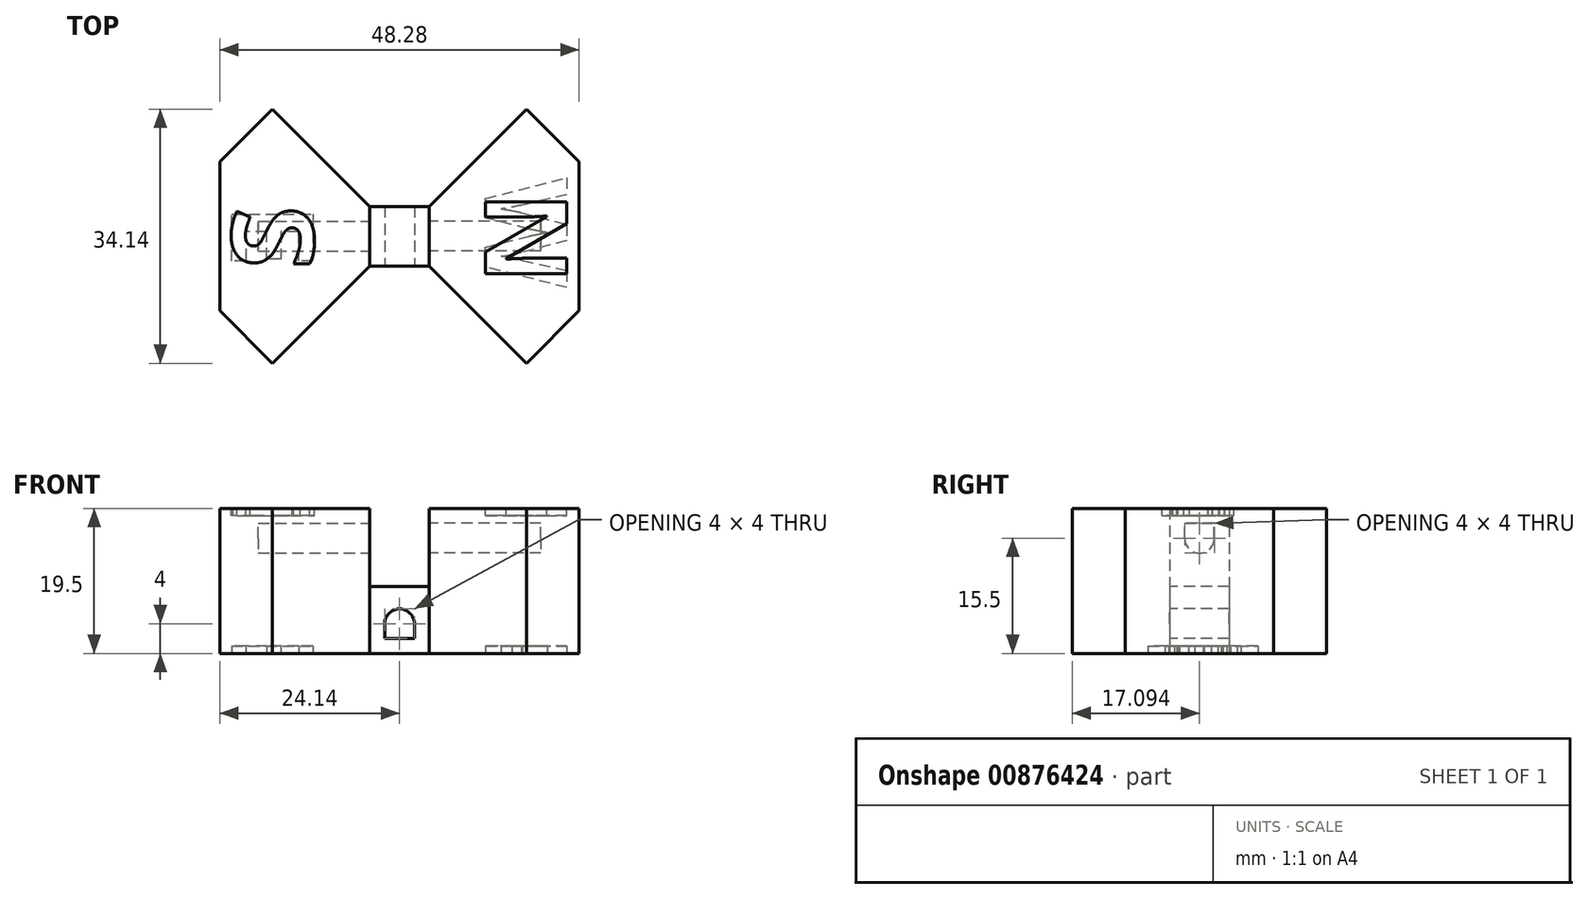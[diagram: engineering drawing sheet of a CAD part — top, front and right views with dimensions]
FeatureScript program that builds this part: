
annotation { "Feature Type Name" : "Feature", "Feature Type Description" : "" }
export const myFeature = defineFeature(function(context is Context, id is Id, definition is map)
    precondition{}
    {
        {
            var Q0;
            Q0=qCreatedBy(makeId("Top.planeOp"),FACE);
            var sketch = newSketch(context, id + "F0", { "sketchPlane" : qUnion([Q0])});
            skCircle(sketch, "E0.cCircle", {"center": v(0, 0) * mm, "radius": 24.14 * mm, "construction": true});
            skLineSegment(sketch, "E0.0", {"start": v(-24.14, 10) * mm, "end": v(-10, 24.14) * mm});
            skLineSegment(sketch, "E0.1", {"start": v(-10, 24.14) * mm, "end": v(10, 24.14) * mm});
            skLineSegment(sketch, "E0.2", {"start": v(10, 24.14) * mm, "end": v(24.14, 10) * mm});
            skLineSegment(sketch, "E0.3", {"start": v(24.14, 10) * mm, "end": v(24.14, -10) * mm});
            skLineSegment(sketch, "E0.4", {"start": v(24.14, -10) * mm, "end": v(10, -24.14) * mm});
            skLineSegment(sketch, "E0.5", {"start": v(10, -24.14) * mm, "end": v(-10, -24.14) * mm});
            skLineSegment(sketch, "E0.6", {"start": v(-10, -24.14) * mm, "end": v(-24.14, -10) * mm});
            skLineSegment(sketch, "E0.7", {"start": v(-24.14, -10) * mm, "end": v(-24.14, 10) * mm});
            skPoint(sketch, "E0.0.midPoint", {"position": v(-17.07, 17.07) * mm});
            skPoint(sketch, "E1", {"position": v(-17.07, -17.07) * mm});
            skPoint(sketch, "E2", {"position": v(17.07, 17.07) * mm});
            skPoint(sketch, "E3", {"position": v(17.07, -17.07) * mm});
            skLineSegment(sketch, "E4", {"start": v(-17.07, 17.07) * mm, "end": v(17.07, -17.07) * mm});
            skLineSegment(sketch, "E5", {"start": v(17.07, 17.07) * mm, "end": v(-17.07, -17.07) * mm});
            skPoint(sketch, "E6", {"position": v(0, 24.14) * mm});
            skPoint(sketch, "E7", {"position": v(24.14, 0) * mm});
            skPoint(sketch, "E8", {"position": v(0, -24.14) * mm});
            skLineSegment(sketch, "E9.bottom", {"start": v(-4, 4) * mm, "end": v(4, 4) * mm});
            skLineSegment(sketch, "E9.top", {"start": v(-4, -4) * mm, "end": v(4, -4) * mm});
            skLineSegment(sketch, "E9.left", {"start": v(-4, 4) * mm, "end": v(-4, -4) * mm});
            skLineSegment(sketch, "E9.right", {"start": v(4, 4) * mm, "end": v(4, -4) * mm});
            skPoint(sketch, "E10", {"position": v(0, 4) * mm});
            skPoint(sketch, "E11", {"position": v(-4, 0) * mm});
            skLineSegment(sketch, "E12", {"start": v(17.07, -17.07) * mm, "end": v(17.07, 17.07) * mm, "construction": true});
            skPoint(sketch, "E13", {"position": v(17.07, 0) * mm});
            skLineSegment(sketch, "E14", {"start": v(-17.07, -17.07) * mm, "end": v(-17.07, 17.07) * mm, "construction": true});
            skPoint(sketch, "E15", {"position": v(-17.07, 0) * mm});
            skSolve(sketch);
        }
        {
            var Q0;
            {var subQ4=sQuery(id+"F0.wireOp",EDGE,"E0.7");Q0=makeQuery(id+"F0.imprint","IMPRINT",FACE,{"disambiguationData":[TD([[makeQuery(id+"F0.imprint","IMPRINT",EDGE,{"derivedFrom":subQ4}),-1.0]])]});}
            var Q1;
            {var subQ1=sQuery(id+"F0.wireOp",EDGE,"E0.3");Q1=makeQuery(id+"F0.imprint","IMPRINT",FACE,{"disambiguationData":[TD([[makeQuery(id+"F0.imprint","IMPRINT",EDGE,{"derivedFrom":subQ1}),-1.0]])]});}
            extrude(context, id + "F1", {"entities" : qUnion([Q0, Q1]), "depth" : 19.5 * mm, "offsetDistance" : 25 * mm});
        }
        {
            var Q0;
            {var subQ0=sQuery(id+"F0.wireOp",EDGE,"E9.right");Q0=makeQuery(id+"F0.imprint","IMPRINT",FACE,{"disambiguationData":[TD([[makeQuery(id+"F0.imprint","IMPRINT",EDGE,{"derivedFrom":subQ0}),-1.0]])]});}
            var Q1;
            {var subQ0=sQuery(id+"F0.wireOp",EDGE,"E9.bottom");Q1=makeQuery(id+"F0.imprint","IMPRINT",FACE,{"disambiguationData":[TD([[makeQuery(id+"F0.imprint","IMPRINT",EDGE,{"derivedFrom":subQ0}),-1.0]])]});}
            var Q2;
            {var subQ0=sQuery(id+"F0.wireOp",EDGE,"E9.left");Q2=makeQuery(id+"F0.imprint","IMPRINT",FACE,{"disambiguationData":[TD([[makeQuery(id+"F0.imprint","IMPRINT",EDGE,{"derivedFrom":subQ0}),1.0]])]});}
            var Q3;
            {var subQ0=sQuery(id+"F0.wireOp",EDGE,"E9.top");Q3=makeQuery(id+"F0.imprint","IMPRINT",FACE,{"disambiguationData":[TD([[makeQuery(id+"F0.imprint","IMPRINT",EDGE,{"derivedFrom":subQ0}),1.0]])]});}
            extrude(context, id + "F2", {"entities" : qUnion([Q0, Q1, Q2, Q3]), "depth" : 9 * mm, "offsetDistance" : 25 * mm});
        }
        {
            var Q0;
            Q0=makeQuery(id+"F2.opExtrude","SWEPT_FACE",FACE,{"disambiguationData":[OSD([sQuery(id+"F0.wireOp",EDGE,"E9.top")])]});
            var sketch = newSketch(context, id + "F3", { "sketchPlane" : qUnion([Q0])});
            skLineSegment(sketch, "E16.bottom", {"start": v(-2, 4) * mm, "end": v(2, 4) * mm});
            skLineSegment(sketch, "E16.top", {"start": v(-2, 0) * mm, "end": v(2, 0) * mm});
            skLineSegment(sketch, "E16.left", {"start": v(-2, 4) * mm, "end": v(-2, 0) * mm});
            skLineSegment(sketch, "E16.right", {"start": v(2, 4) * mm, "end": v(2, 0) * mm});
            skPoint(sketch, "E17", {"position": v(0, 0) * mm});
            skPoint(sketch, "E18", {"position": v(0, 4) * mm});
            skPoint(sketch, "E19", {"position": v(0, 9) * mm});
            skLineSegment(sketch, "E20", {"start": v(0, 9) * mm, "end": v(0, 0) * mm});
            skLineSegment(sketch, "E21", {"start": v(0, 4) * mm, "end": v(0, 0) * mm});
            skPoint(sketch, "E22", {"position": v(-2, 2) * mm});
            skPoint(sketch, "E23", {"position": v(2, 2) * mm});
            skArc(sketch, "E24", {"start": v(2, 4) * mm, "mid": v(0, 6) * mm, "end": v(-2, 4) * mm});
            skLineSegment(sketch, "E25", {"start": v(-2, 2) * mm, "end": v(2, 2) * mm});
            skSolve(sketch);
        }
        {
            var Q0;
            {var subQ0=sQuery(id+"F3.wireOp",EDGE,"E16.right");var subQ5=sQuery(id+"F3.wireOp",EDGE,"E25");var subQ6=makeQuery(id+"F3.imprint","INTERSECT",VERTEX,{"derivedFrom":[subQ0,subQ5]});Q0=makeQuery(id+"F3.imprint","IMPRINT",FACE,{"disambiguationData":[TD([[makeQuery(id+"F3.imprint","IMPRINT",EDGE,{"disambiguationData":[TD([[subQ6,1.0]])],"derivedFrom":subQ5}),1.0]])]});}
            var Q1;
            {var subQ0=sQuery(id+"F3.wireOp",EDGE,"E16.left");var subQ5=sQuery(id+"F3.wireOp",EDGE,"E25");var subQ7=makeQuery(id+"F3.imprint","INTERSECT",VERTEX,{"derivedFrom":[subQ0,subQ5]});Q1=makeQuery(id+"F3.imprint","IMPRINT",FACE,{"disambiguationData":[TD([[makeQuery(id+"F3.imprint","IMPRINT",EDGE,{"disambiguationData":[TD([[subQ7,-1.0]])],"derivedFrom":subQ5}),1.0]])]});}
            var Q2;
            {var subQ0=sQuery(id+"F3.wireOp",EDGE,"E24");var subQ3=sQuery(id+"F3.wireOp",EDGE,"E20");var subQ5=makeQuery(id+"F3.imprint","INTERSECT",VERTEX,{"derivedFrom":[subQ3,subQ0]});Q2=makeQuery(id+"F3.imprint","IMPRINT",FACE,{"disambiguationData":[TD([[makeQuery(id+"F3.imprint","IMPRINT",EDGE,{"disambiguationData":[TD([[subQ5,-1.0]])],"derivedFrom":subQ3}),-1.0]])]});}
            var Q3;
            {var subQ0=sQuery(id+"F3.wireOp",EDGE,"E24");var subQ3=sQuery(id+"F3.wireOp",EDGE,"E20");var subQ5=makeQuery(id+"F3.imprint","INTERSECT",VERTEX,{"derivedFrom":[subQ3,subQ0]});Q3=makeQuery(id+"F3.imprint","IMPRINT",FACE,{"disambiguationData":[TD([[makeQuery(id+"F3.imprint","IMPRINT",EDGE,{"disambiguationData":[TD([[subQ5,-1.0]])],"derivedFrom":subQ3}),1.0]])]});}
            extrude(context, id + "F4", {"entities" : qUnion([Q0, Q1, Q2, Q3]), "operationType" : NewBodyOperationType.REMOVE, "oppositeDirection" : true, "depth" : 8 * mm, "offsetDistance" : 25 * mm});
        }
        {
            var Q0;
            Q0=makeQuery(id+"F1.opExtrude","SWEPT_FACE",FACE,{"disambiguationData":[OSD([sQuery(id+"F0.wireOp",EDGE,"E9.left")])]});
            var sketch = newSketch(context, id + "F5", { "sketchPlane" : qUnion([Q0])});
            skLineSegment(sketch, "E26.bottom", {"start": v(2.02, 15.5) * mm, "end": v(-1.98, 15.5) * mm});
            skLineSegment(sketch, "E26.top", {"start": v(2.02, 19.5) * mm, "end": v(-1.98, 19.5) * mm});
            skLineSegment(sketch, "E26.left", {"start": v(2.02, 15.5) * mm, "end": v(2.02, 19.5) * mm});
            skLineSegment(sketch, "E26.right", {"start": v(-1.98, 15.5) * mm, "end": v(-1.98, 19.5) * mm});
            skPoint(sketch, "E27", {"position": v(0.02, 19.5) * mm});
            skPoint(sketch, "E28", {"position": v(0.02, 15.5) * mm});
            skPoint(sketch, "E29", {"position": v(0.02, 10.5) * mm});
            skLineSegment(sketch, "E30", {"start": v(0.02, 10.5) * mm, "end": v(0.02, 19.5) * mm});
            skLineSegment(sketch, "E31", {"start": v(0.02, 15.5) * mm, "end": v(0.02, 19.5) * mm});
            skPoint(sketch, "E32", {"position": v(2.02, 17.5) * mm});
            skPoint(sketch, "E33", {"position": v(-1.98, 17.5) * mm});
            skArc(sketch, "E34", {"start": v(-1.98, 15.5) * mm, "mid": v(0.02, 13.5) * mm, "end": v(2.02, 15.5) * mm});
            skLineSegment(sketch, "E35", {"start": v(2.02, 17.5) * mm, "end": v(-1.98, 17.5) * mm});
            skSolve(sketch);
        }
        {
            var Q0;
            {var subQ0=sQuery(id+"F5.wireOp",EDGE,"E26.right");var subQ5=sQuery(id+"F5.wireOp",EDGE,"E35");var subQ6=makeQuery(id+"F5.imprint","INTERSECT",VERTEX,{"derivedFrom":[subQ0,subQ5]});Q0=makeQuery(id+"F5.imprint","IMPRINT",FACE,{"disambiguationData":[TD([[makeQuery(id+"F5.imprint","IMPRINT",EDGE,{"disambiguationData":[TD([[subQ6,1.0]])],"derivedFrom":subQ5}),1.0]])]});}
            var Q1;
            {var subQ0=sQuery(id+"F5.wireOp",EDGE,"E26.left");var subQ5=sQuery(id+"F5.wireOp",EDGE,"E35");var subQ6=makeQuery(id+"F5.imprint","INTERSECT",VERTEX,{"derivedFrom":[subQ0,subQ5]});Q1=makeQuery(id+"F5.imprint","IMPRINT",FACE,{"disambiguationData":[TD([[makeQuery(id+"F5.imprint","IMPRINT",EDGE,{"disambiguationData":[TD([[subQ6,-1.0]])],"derivedFrom":subQ5}),1.0]])]});}
            var Q2;
            {var subQ0=sQuery(id+"F5.wireOp",EDGE,"E34");var subQ3=sQuery(id+"F5.wireOp",EDGE,"E30");var subQ5=makeQuery(id+"F5.imprint","INTERSECT",VERTEX,{"derivedFrom":[subQ3,subQ0]});Q2=makeQuery(id+"F5.imprint","IMPRINT",FACE,{"disambiguationData":[TD([[makeQuery(id+"F5.imprint","IMPRINT",EDGE,{"disambiguationData":[TD([[subQ5,-1.0]])],"derivedFrom":subQ3}),1.0]])]});}
            var Q3;
            {var subQ0=sQuery(id+"F5.wireOp",EDGE,"E34");var subQ3=sQuery(id+"F5.wireOp",EDGE,"E30");var subQ5=makeQuery(id+"F5.imprint","INTERSECT",VERTEX,{"derivedFrom":[subQ3,subQ0]});Q3=makeQuery(id+"F5.imprint","IMPRINT",FACE,{"disambiguationData":[TD([[makeQuery(id+"F5.imprint","IMPRINT",EDGE,{"disambiguationData":[TD([[subQ5,-1.0]])],"derivedFrom":subQ3}),-1.0]])]});}
            extrude(context, id + "F6", {"entities" : qUnion([Q0, Q1, Q2, Q3]), "operationType" : NewBodyOperationType.REMOVE, "oppositeDirection" : true, "depth" : 15 * mm, "offsetDistance" : 25 * mm});
        }
        {
            var Q0;
            Q0=makeQuery(id+"F1.opExtrude","SWEPT_FACE",FACE,{"disambiguationData":[OSD([sQuery(id+"F0.wireOp",EDGE,"E9.right")])]});
            var sketch = newSketch(context, id + "F7", { "sketchPlane" : qUnion([Q0])});
            skLineSegment(sketch, "E36.bottom", {"start": v(2, 15.5) * mm, "end": v(-2, 15.5) * mm});
            skLineSegment(sketch, "E36.top", {"start": v(2, 19.5) * mm, "end": v(-2, 19.5) * mm});
            skLineSegment(sketch, "E36.left", {"start": v(2, 15.5) * mm, "end": v(2, 19.5) * mm});
            skLineSegment(sketch, "E36.right", {"start": v(-2, 15.5) * mm, "end": v(-2, 19.5) * mm});
            skPoint(sketch, "E37", {"position": v(0, 19.5) * mm});
            skPoint(sketch, "E38", {"position": v(0, 15.5) * mm});
            skPoint(sketch, "E39", {"position": v(-2.46, 10.5) * mm});
            skLineSegment(sketch, "E40", {"start": v(-2.46, 10.5) * mm, "end": v(-2.46, 19.5) * mm});
            skLineSegment(sketch, "E41", {"start": v(0, 15.5) * mm, "end": v(0, 19.5) * mm});
            skPoint(sketch, "E42", {"position": v(2, 17.5) * mm});
            skPoint(sketch, "E43", {"position": v(-2, 17.5) * mm});
            skArc(sketch, "E44", {"start": v(-2, 15.5) * mm, "mid": v(0, 13.5) * mm, "end": v(2, 15.5) * mm});
            skLineSegment(sketch, "E45", {"start": v(2, 17.5) * mm, "end": v(-2, 17.5) * mm});
            skSolve(sketch);
        }
        {
            var Q0;
            {var subQ1=sQuery(id+"F7.wireOp",EDGE,"E36.bottom");var subQ3=sQuery(id+"F7.wireOp",EDGE,"E41");var subQ4=makeQuery(id+"F7.imprint","INTERSECT",VERTEX,{"derivedFrom":[subQ1,subQ3]});Q0=makeQuery(id+"F7.imprint","IMPRINT",FACE,{"disambiguationData":[TD([[makeQuery(id+"F7.imprint","IMPRINT",EDGE,{"disambiguationData":[TD([[subQ4,-1.0]])],"derivedFrom":subQ3}),-1.0]])]});}
            var Q1;
            {var subQ1=sQuery(id+"F7.wireOp",EDGE,"E36.bottom");var subQ3=sQuery(id+"F7.wireOp",EDGE,"E41");var subQ4=makeQuery(id+"F7.imprint","INTERSECT",VERTEX,{"derivedFrom":[subQ1,subQ3]});Q1=makeQuery(id+"F7.imprint","IMPRINT",FACE,{"disambiguationData":[TD([[makeQuery(id+"F7.imprint","IMPRINT",EDGE,{"disambiguationData":[TD([[subQ4,-1.0]])],"derivedFrom":subQ3}),1.0]])]});}
            var Q2;
            {var subQ0=sQuery(id+"F7.wireOp",EDGE,"E44");Q2=makeQuery(id+"F7.imprint","IMPRINT",FACE,{"disambiguationData":[TD([[makeQuery(id+"F7.imprint","IMPRINT",EDGE,{"derivedFrom":subQ0}),1.0]])]});}
            extrude(context, id + "F8", {"entities" : qUnion([Q0, Q1, Q2]), "operationType" : NewBodyOperationType.REMOVE, "oppositeDirection" : true, "depth" : 15 * mm, "offsetDistance" : 25 * mm});
        }
        {
            var Q0;
            Q0=makeQuery(id+"F1.opExtrude","CAP_FACE",FACE,{"disambiguationData":[OSD([sQuery(id+"F0.wireOp",EDGE,"E0.2"),sQuery(id+"F0.wireOp",EDGE,"E0.3"),sQuery(id+"F0.wireOp",EDGE,"E0.4"),sQuery(id+"F0.wireOp",EDGE,"E4"),sQuery(id+"F0.wireOp",EDGE,"E5"),sQuery(id+"F0.wireOp",EDGE,"E9.right")])],"isStart":false});
            var sketch = newSketch(context, id + "F9", { "sketchPlane" : qUnion([Q0])});
            skText(sketch, "E46", { "text": "N", "fontName": "OpenSans-Bold.ttf"});
            skLineSegment(sketch, "E47", {"start": v(17.07, 17.07) * mm, "end": v(17.07, -17.07) * mm});
            skPoint(sketch, "E48", {"position": v(17.07, 0) * mm});
            const initialGuessF9  = {"E46": [0.01157, 0.00602, 0, -1, 0.011]};
            skSetInitialGuess(sketch, initialGuessF9);
            skSolve(sketch);
        }
        {
            var Q0;
            {var subQ4=sQuery(id+"F9.wireOp",EDGE,"E46.sketch_text.stroke-4");Q0=makeQuery(id+"F9.imprint","IMPRINT",FACE,{"disambiguationData":[TD([[makeQuery(id+"F9.imprint","IMPRINT",EDGE,{"derivedFrom":subQ4}),-1.0]])]});}
            var Q1;
            {var subQ5=sQuery(id+"F9.wireOp",EDGE,"E46.sketch_text.stroke-2");Q1=makeQuery(id+"F9.imprint","IMPRINT",FACE,{"disambiguationData":[TD([[makeQuery(id+"F9.imprint","IMPRINT",EDGE,{"derivedFrom":subQ5}),-1.0]])]});}
            var Q2;
            {var subQ5=sQuery(id+"F9.wireOp",EDGE,"E46.sketch_text.stroke-0");Q2=makeQuery(id+"F9.imprint","IMPRINT",FACE,{"disambiguationData":[TD([[makeQuery(id+"F9.imprint","IMPRINT",EDGE,{"derivedFrom":subQ5}),-1.0]])]});}
            var Q3;
            {var subQ4=sQuery(id+"F9.wireOp",EDGE,"E46.sketch_text.stroke-11");Q3=makeQuery(id+"F9.imprint","IMPRINT",FACE,{"disambiguationData":[TD([[makeQuery(id+"F9.imprint","IMPRINT",EDGE,{"derivedFrom":subQ4}),-1.0]])]});}
            extrude(context, id + "F10", {"entities" : qUnion([Q0, Q1, Q2, Q3]), "operationType" : NewBodyOperationType.REMOVE, "oppositeDirection" : true, "depth" : 1 * mm, "offsetDistance" : 25 * mm});
        }
        {
            var Q0;
            Q0=makeQuery(id+"F1.opExtrude","CAP_FACE",FACE,{"disambiguationData":[OSD([sQuery(id+"F0.wireOp",EDGE,"E0.0"),sQuery(id+"F0.wireOp",EDGE,"E0.6"),sQuery(id+"F0.wireOp",EDGE,"E0.7"),sQuery(id+"F0.wireOp",EDGE,"E4"),sQuery(id+"F0.wireOp",EDGE,"E5"),sQuery(id+"F0.wireOp",EDGE,"E9.left")])],"isStart":false});
            var sketch = newSketch(context, id + "F11", { "sketchPlane" : qUnion([Q0])});
            skText(sketch, "E49", { "text": "S", "fontName": "OpenSans-Bold.ttf"});
            skLineSegment(sketch, "E50", {"start": v(-17.07, 17.07) * mm, "end": v(-17.07, -17.07) * mm, "construction": true});
            skPoint(sketch, "E51", {"position": v(-17.07, 0) * mm});
            const initialGuessF11  = {"E49": [-0.01157, -0.0044, 0, 1, 0.011]};
            skSetInitialGuess(sketch, initialGuessF11);
            skSolve(sketch);
        }
        {
            var Q0;
            Q0 = qSketchRegion(id + "F11", true);
            extrude(context, id + "F12", {"entities" : qUnion([Q0]), "operationType" : NewBodyOperationType.REMOVE, "oppositeDirection" : true, "depth" : 1 * mm, "offsetDistance" : 25 * mm});
        }
        {
            var Q0;
            {var subQ1=sQuery(id+"F0.wireOp",EDGE,"E0.3");Q0=makeQuery(id+"F0.imprint","IMPRINT",FACE,{"disambiguationData":[TD([[makeQuery(id+"F0.imprint","IMPRINT",EDGE,{"derivedFrom":subQ1}),-1.0]])]});}
            var sketch = newSketch(context, id + "F13", { "sketchPlane" : qUnion([Q0])});
            skText(sketch, "E52", { "text": "W", "fontName": "OpenSans-Bold.ttf"});
            skPoint(sketch, "E53", {"position": v(17.07, 0) * mm});
            const initialGuessF13  = {"E52": [0.01157, 0.00788, 0, -1, 0.011]};
            skSetInitialGuess(sketch, initialGuessF13);
            skSolve(sketch);
        }
        {
            var Q0;
            Q0 = qSketchRegion(id + "F13", true);
            extrude(context, id + "F14", {"entities" : qUnion([Q0]), "operationType" : NewBodyOperationType.REMOVE, "depth" : 1 * mm, "offsetDistance" : 25 * mm});
        }
        {
            var Q0;
            {var subQ4=sQuery(id+"F0.wireOp",EDGE,"E0.7");Q0=makeQuery(id+"F0.imprint","IMPRINT",FACE,{"disambiguationData":[TD([[makeQuery(id+"F0.imprint","IMPRINT",EDGE,{"derivedFrom":subQ4}),-1.0]])]});}
            var sketch = newSketch(context, id + "F15", { "sketchPlane" : qUnion([Q0])});
            skText(sketch, "E54", { "text": "E", "fontName": "OpenSans-Bold.ttf"});
            skPoint(sketch, "E55", {"position": v(-17.07, 0) * mm});
            const initialGuessF15  = {"E54": [-0.02257, 0.00432, 0, -1, 0.011]};
            skSetInitialGuess(sketch, initialGuessF15);
            skSolve(sketch);
        }
        {
            var Q0;
            Q0 = qSketchRegion(id + "F15", true);
            extrude(context, id + "F16", {"entities" : qUnion([Q0]), "operationType" : NewBodyOperationType.REMOVE, "depth" : 1 * mm, "offsetDistance" : 25 * mm});
        }
    });
